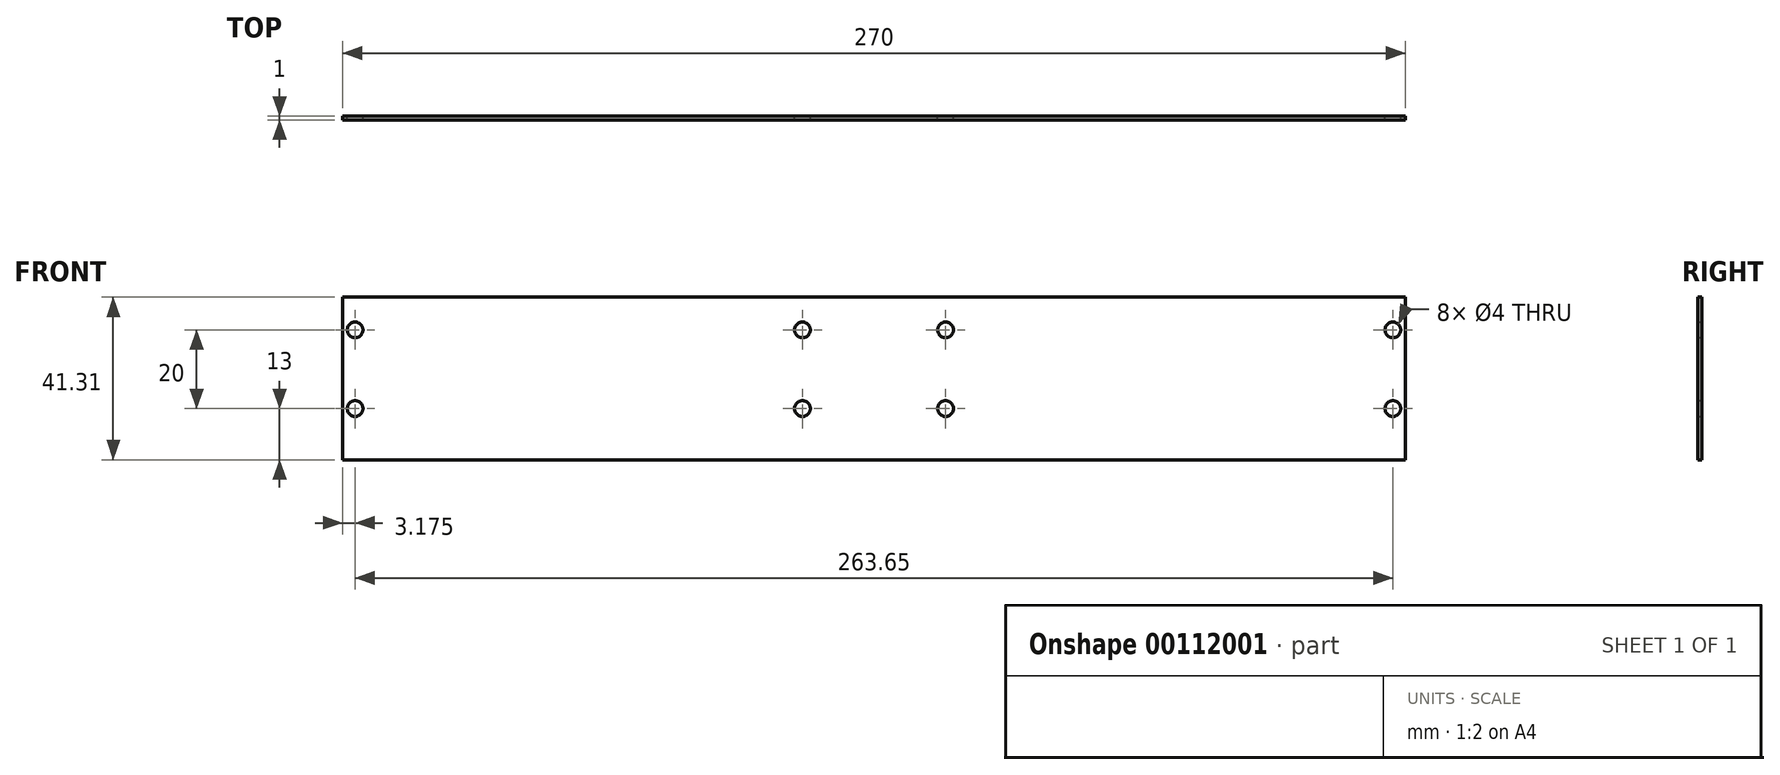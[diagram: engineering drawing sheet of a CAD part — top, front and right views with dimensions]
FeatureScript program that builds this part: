
annotation { "Feature Type Name" : "Feature", "Feature Type Description" : "" }
export const myFeature = defineFeature(function(context is Context, id is Id, definition is map)
    precondition{}
    {
        {
            var Q0;
            Q0=qCreatedBy(makeId("Front.planeOp"),FACE);
            var sketch = newSketch(context, id + "F0", { "sketchPlane" : qUnion([Q0])});
            skLineSegment(sketch, "E0.bottom", {"start": v(0, 0) * mm, "end": v(270, 0) * mm});
            skLineSegment(sketch, "E0.top", {"start": v(0, 41.31) * mm, "end": v(270, 41.31) * mm});
            skLineSegment(sketch, "E0.left", {"start": v(0, 0) * mm, "end": v(0, 41.31) * mm});
            skLineSegment(sketch, "E0.right", {"start": v(270, 0) * mm, "end": v(270, 41.31) * mm});
            skLineSegment(sketch, "E1", {"start": v(135, 41.31) * mm, "end": v(135, 0) * mm, "construction": true});
            skLineSegment(sketch, "E2.bottom", {"start": v(3.18, 33) * mm, "end": v(266.82, 33) * mm, "construction": true});
            skLineSegment(sketch, "E2.top", {"start": v(3.18, 13) * mm, "end": v(266.82, 13) * mm, "construction": true});
            skLineSegment(sketch, "E2.left", {"start": v(3.17, 33) * mm, "end": v(3.18, 13) * mm, "construction": true});
            skLineSegment(sketch, "E2.right", {"start": v(266.82, 33) * mm, "end": v(266.82, 13) * mm, "construction": true});
            skCircle(sketch, "E3", {"center": v(3.17, 33) * mm, "radius": 2 * mm});
            skCircle(sketch, "E4", {"center": v(3.18, 13) * mm, "radius": 2 * mm});
            skCircle(sketch, "E5", {"center": v(266.82, 33) * mm, "radius": 2 * mm});
            skCircle(sketch, "E6", {"center": v(266.82, 13) * mm, "radius": 2 * mm});
            skCircle(sketch, "E7", {"center": v(153.17, 33) * mm, "radius": 2 * mm});
            skCircle(sketch, "E8", {"center": v(153.17, 13) * mm, "radius": 2 * mm});
            skCircle(sketch, "E9", {"center": v(116.82, 13) * mm, "radius": 2 * mm});
            skCircle(sketch, "E10", {"center": v(116.82, 33) * mm, "radius": 2 * mm});
            skPoint(sketch, "E11", {"position": v(135, 33) * mm});
            skLineSegment(sketch, "E12", {"start": v(116.82, 33) * mm, "end": v(135, 23) * mm, "construction": true});
            skLineSegment(sketch, "E13", {"start": v(135, 23) * mm, "end": v(153.17, 13) * mm, "construction": true});
            skSolve(sketch);
        }
        {
            var Q0;
            Q0 = qSketchRegion(id + "F0", true);
            extrude(context, id + "F1", {"entities" : qUnion([Q0]), "depth" : 1 * mm});
        }
    });
